# Revit family: P710027-020
name_source: partatom
category: Lighting Fixtures
revit_build: Autodesk Revit 2014 (Build: 20130308_1515(x64)
units: mm (PartAtom-declared; Revit-internal decimal feet)

## types (1)
- P710027-020
    Apparent Load = 120 VA
    Assembly Code = D5020200
    Connector Description = Lighting Connector
    Default Elevation = 48"
    Depth = 3 7/8"
    Description = An iconic fixture, Astra features an organic, asymmetrical design. Ideal for dining room settings or entryways, these space-aged inspired pieces are so versatile they can be incorporated into a variety of interiors. Wall Bracket. Antique Bronze finish.
    Features = An iconic style design that adds dynamic flair to any room
• Versatile space-aged inspired pieces that can be incorporated into a
variety of interiors
• Antique Bronze finish
• Wall bracket uses two 60W medium base bulbs (sold separately)
• Ideal for hallways, foyers and entranceways
• Progress Lighting Design Series, a collection offering fashionable styles
and affordable luxury
    Fixture distribution = Direct
    Glass = Hubbell - Glass
    Gold = Hubbell - Gold
    Height = 17 3/4"
    Housing Material = Paint - Hubbell - Textured Camera Black
    Lamp = LED
    Load Classification = Lighting
    Manufacturer = Progress Lighting
    Model = P710027-020
    Power Factor = 1
    Product Documentation Link = https://hubbellcdn.com
    Product Link = https://www.hubbell.com
    URL = https://www.hubbell.com
    Voltage = 120 V
    Warranty = 5 years Warranty
    Wattage Comments = 120W
    Watts = 120 W
    Width = 7 1/4"

## geometry (parser evidence)
native form markers: Sweep x6
no freeform markers — native parametric forms only
